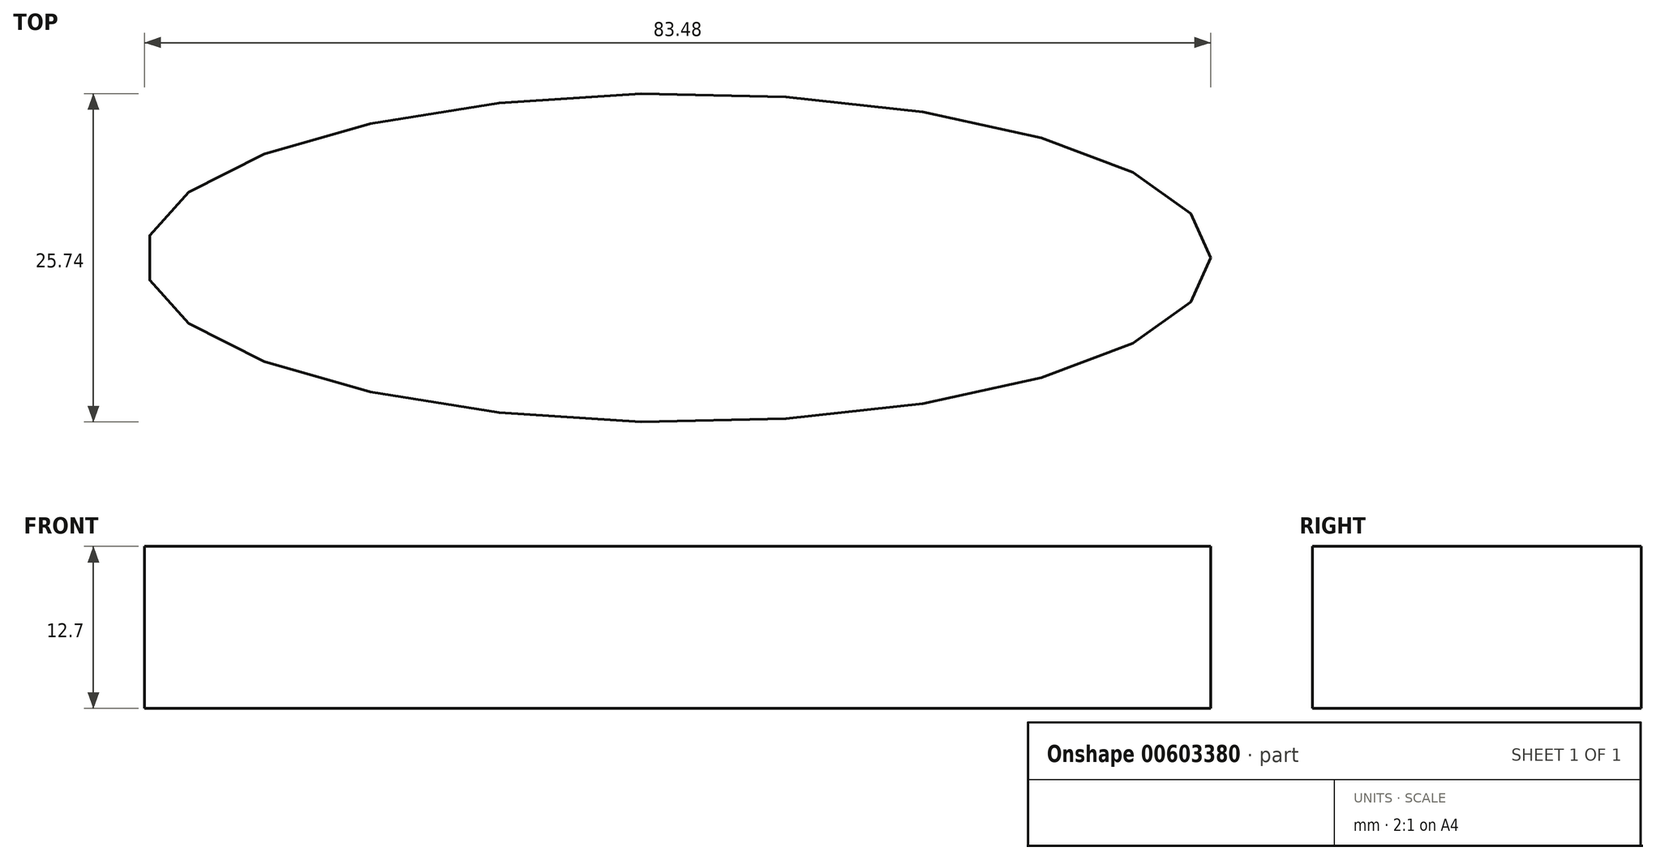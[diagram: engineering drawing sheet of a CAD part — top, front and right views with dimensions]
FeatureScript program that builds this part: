
annotation { "Feature Type Name" : "Feature", "Feature Type Description" : "" }
export const myFeature = defineFeature(function(context is Context, id is Id, definition is map)
    precondition{}
    {
        {
            var Q0;
            Q0=qCreatedBy(makeId("Top.planeOp"),FACE);
            var sketch = newSketch(context, id + "F0", { "sketchPlane" : qUnion([Q0])});
            skEllipse(sketch, "E0", {"center": v(-30.39, 0) * mm, "majorRadius": 41.74 * mm, "minorRadius": 12.87 * mm, "majorAxis": v(1, 0)});
            skSolve(sketch);
        }
        {
            var Q0;
            Q0 = qSketchRegion(id + "F0", true);
            extrude(context, id + "F1", {"entities" : qUnion([Q0]), "depth" : 12.7 * mm, "offsetDistance" : 25.4 * mm});
        }
    });
